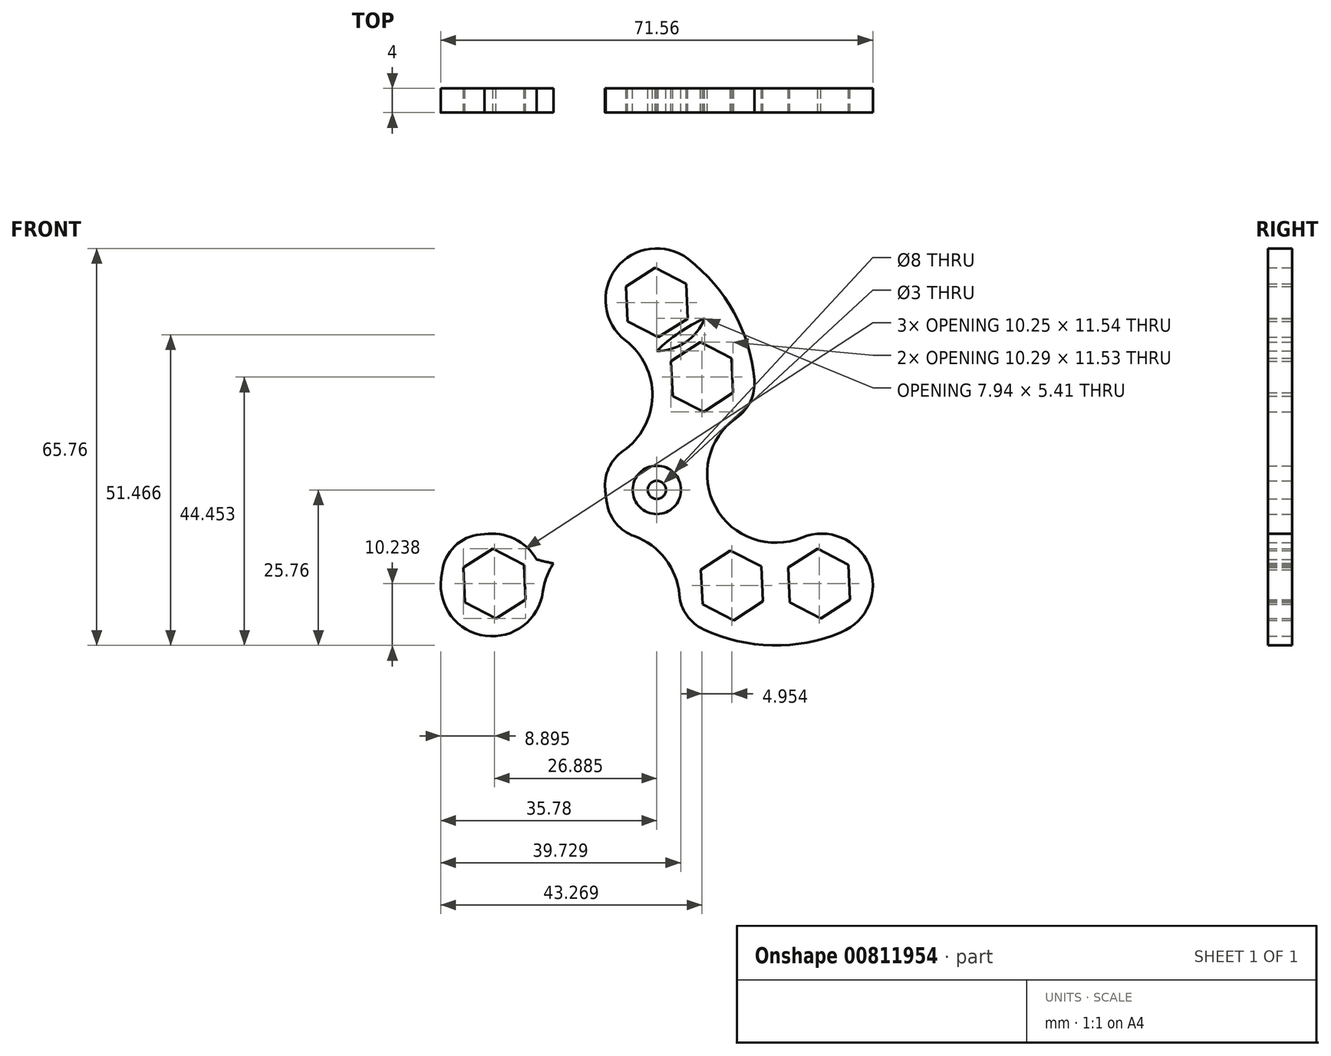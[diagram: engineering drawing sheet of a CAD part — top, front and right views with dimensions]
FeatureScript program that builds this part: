
annotation { "Feature Type Name" : "Feature", "Feature Type Description" : "" }
export const myFeature = defineFeature(function(context is Context, id is Id, definition is map)
    precondition{}
    {
        {
            var Q0;
            Q0=qCreatedBy(makeId("Front.planeOp"),FACE);
            var sketch = newSketch(context, id + "F0", { "sketchPlane" : qUnion([Q0])});
            skCircle(sketch, "E0", {"center": v(0, 0) * mm, "radius": 4 * mm});
            skCircle(sketch, "E1", {"center": v(0, 0) * mm, "radius": 1.5 * mm});
            skCircle(sketch, "E2", {"center": v(0, 0) * mm, "radius": 40 * mm, "construction": true});
            skCircle(sketch, "E3", {"center": v(0, 31.5) * mm, "radius": 8.5 * mm});
            skCircle(sketch, "E4", {"center": v(0, 0) * mm, "radius": 8.5 * mm});
            skCircle(sketch, "E5", {"center": v(-12.1, 15.75) * mm, "radius": 11.36 * mm});
            skCircle(sketch, "E6", {"center": v(-12.1, 15.75) * mm, "radius": 28.36 * mm});
            skCircle(sketch, "E7.1.0", {"center": v(-27.28, -15.75) * mm, "radius": 8.5 * mm});
            skCircle(sketch, "E7.2.0", {"center": v(27.28, -15.75) * mm, "radius": 8.5 * mm});
            skCircle(sketch, "E8.1.0", {"center": v(-7.59, -18.36) * mm, "radius": 11.36 * mm});
            skCircle(sketch, "E8.2.0", {"center": v(19.7, 2.6) * mm, "radius": 11.36 * mm});
            skCircle(sketch, "E9.1.0", {"center": v(-7.59, -18.36) * mm, "radius": 28.36 * mm});
            skCircle(sketch, "E9.2.0", {"center": v(19.7, 2.6) * mm, "radius": 28.36 * mm});
            skSolve(sketch);
        }
        {
            var Q0;
            Q0=makeQuery(id+"F0.imprint","IMPRINT",FACE,{"disambiguationData":[TD([[makeQuery(id+"F0.imprint","IMPRINT",EDGE,{"derivedFrom":sQuery(id+"F0.wireOp",EDGE,"E0")}),1.0]])]});
            extrude(context, id + "F1", {"entities" : qUnion([Q0]), "depth" : 4 * mm, "offsetDistance" : 25 * mm});
        }
        {
            var Q0;
            {var subQ0=sQuery(id+"F0.wireOp",EDGE,"E9.1.0");var subQ1=sQuery(id+"F0.wireOp",EDGE,"E4");var subQ2=makeQuery(id+"F0.imprint","INTERSECT",VERTEX,{"derivedFrom":[subQ1,subQ0]});Q0=makeQuery(id+"F0.imprint","IMPRINT",FACE,{"disambiguationData":[TD([[makeQuery(id+"F0.imprint","IMPRINT",EDGE,{"disambiguationData":[TD([[subQ2,1.0]])],"derivedFrom":subQ1}),-1.0]])]});}
            var Q1;
            {var subQ0=sQuery(id+"F0.wireOp",EDGE,"E9.1.0");var subQ1=sQuery(id+"F0.wireOp",EDGE,"E4");var subQ2=makeQuery(id+"F0.imprint","INTERSECT",VERTEX,{"derivedFrom":[subQ1,subQ0]});Q1=makeQuery(id+"F0.imprint","IMPRINT",FACE,{"disambiguationData":[TD([[makeQuery(id+"F0.imprint","IMPRINT",EDGE,{"disambiguationData":[TD([[subQ2,-1.0]])],"derivedFrom":subQ1}),-1.0]])]});}
            var Q2;
            {var subQ0=sQuery(id+"F0.wireOp",EDGE,"E5");var subQ1=sQuery(id+"F0.wireOp",EDGE,"E4");var subQ2=makeQuery(id+"F0.imprint","INTERSECT",VERTEX,{"derivedFrom":[subQ1,subQ0]});Q2=makeQuery(id+"F0.imprint","IMPRINT",FACE,{"disambiguationData":[TD([[makeQuery(id+"F0.imprint","IMPRINT",EDGE,{"disambiguationData":[TD([[subQ2,-1.0]])],"derivedFrom":subQ1}),-1.0]])]});}
            var Q3;
            {var subQ0=sQuery(id+"F0.wireOp",EDGE,"E9.2.0");var subQ1=sQuery(id+"F0.wireOp",EDGE,"E4");var subQ2=makeQuery(id+"F0.imprint","INTERSECT",VERTEX,{"derivedFrom":[subQ1,subQ0]});Q3=makeQuery(id+"F0.imprint","IMPRINT",FACE,{"disambiguationData":[TD([[makeQuery(id+"F0.imprint","IMPRINT",EDGE,{"disambiguationData":[TD([[subQ2,-1.0]])],"derivedFrom":subQ1}),-1.0]])]});}
            var Q4;
            {var subQ0=sQuery(id+"F0.wireOp",EDGE,"E8.1.0");var subQ1=sQuery(id+"F0.wireOp",EDGE,"E4");var subQ2=makeQuery(id+"F0.imprint","INTERSECT",VERTEX,{"derivedFrom":[subQ1,subQ0]});Q4=makeQuery(id+"F0.imprint","IMPRINT",FACE,{"disambiguationData":[TD([[makeQuery(id+"F0.imprint","IMPRINT",EDGE,{"disambiguationData":[TD([[subQ2,-1.0]])],"derivedFrom":subQ1}),-1.0]])]});}
            var Q5;
            {var subQ0=sQuery(id+"F0.wireOp",EDGE,"E8.2.0");var subQ1=sQuery(id+"F0.wireOp",EDGE,"E4");var subQ2=makeQuery(id+"F0.imprint","INTERSECT",VERTEX,{"derivedFrom":[subQ1,subQ0]});Q5=makeQuery(id+"F0.imprint","IMPRINT",FACE,{"disambiguationData":[TD([[makeQuery(id+"F0.imprint","IMPRINT",EDGE,{"disambiguationData":[TD([[subQ2,1.0]])],"derivedFrom":subQ1}),-1.0]])]});}
            var Q6;
            {var subQ6=sQuery(id+"F0.wireOp",EDGE,"E9.2.0");var subQ11=sQuery(id+"F0.wireOp",EDGE,"E3");var subQ12=makeQuery(id+"F0.imprint","INTERSECT",VERTEX,{"disambiguationData":[OD(0.0)],"derivedFrom":[subQ11,subQ6]});Q6=makeQuery(id+"F0.imprint","IMPRINT",FACE,{"disambiguationData":[TD([[makeQuery(id+"F0.imprint","IMPRINT",EDGE,{"disambiguationData":[TD([[subQ12,-1.0]])],"derivedFrom":subQ11}),-1.0]])]});}
            var Q7;
            {var subQ0=sQuery(id+"F0.wireOp",EDGE,"E9.2.0");var subQ1=sQuery(id+"F0.wireOp",EDGE,"E3");var subQ2=makeQuery(id+"F0.imprint","INTERSECT",VERTEX,{"disambiguationData":[OD(0.0)],"derivedFrom":[subQ1,subQ0]});Q7=makeQuery(id+"F0.imprint","IMPRINT",FACE,{"disambiguationData":[TD([[makeQuery(id+"F0.imprint","IMPRINT",EDGE,{"disambiguationData":[TD([[subQ2,-1.0]])],"derivedFrom":subQ1}),1.0]])]});}
            var Q8;
            {var subQ0=sQuery(id+"F0.wireOp",EDGE,"E3");var subQ1=makeQuery(id+"F0.imprint","INTERSECT",VERTEX,{"derivedFrom":[subQ0,sQuery(id+"F0.wireOp",EDGE,"E6")]});Q8=makeQuery(id+"F0.imprint","IMPRINT",FACE,{"disambiguationData":[TD([[makeQuery(id+"F0.imprint","IMPRINT",EDGE,{"disambiguationData":[TD([[subQ1,-1.0]])],"derivedFrom":subQ0}),1.0]])]});}
            var Q9;
            {var subQ0=sQuery(id+"F0.wireOp",EDGE,"E6");var subQ1=sQuery(id+"F0.wireOp",EDGE,"E3");var subQ2=makeQuery(id+"F0.imprint","INTERSECT",VERTEX,{"derivedFrom":[subQ1,subQ0]});Q9=makeQuery(id+"F0.imprint","IMPRINT",FACE,{"disambiguationData":[TD([[makeQuery(id+"F0.imprint","IMPRINT",EDGE,{"disambiguationData":[TD([[subQ2,1.0]])],"derivedFrom":subQ1}),-1.0]])]});}
            var Q10;
            {var subQ0=sQuery(id+"F0.wireOp",EDGE,"E5");var subQ1=sQuery(id+"F0.wireOp",EDGE,"E3");var subQ2=makeQuery(id+"F0.imprint","INTERSECT",VERTEX,{"derivedFrom":[subQ1,subQ0]});Q10=makeQuery(id+"F0.imprint","IMPRINT",FACE,{"disambiguationData":[TD([[makeQuery(id+"F0.imprint","IMPRINT",EDGE,{"disambiguationData":[TD([[subQ2,-1.0]])],"derivedFrom":subQ1}),-1.0]])]});}
            var Q11;
            {var subQ0=sQuery(id+"F0.wireOp",EDGE,"E7.2.0");var subQ1=makeQuery(id+"F0.imprint","INTERSECT",VERTEX,{"derivedFrom":[subQ0,sQuery(id+"F0.wireOp",EDGE,"E9.2.0")]});Q11=makeQuery(id+"F0.imprint","IMPRINT",FACE,{"disambiguationData":[TD([[makeQuery(id+"F0.imprint","IMPRINT",EDGE,{"disambiguationData":[TD([[subQ1,-1.0]])],"derivedFrom":subQ0}),1.0]])]});}
            var Q12;
            {var subQ0=sQuery(id+"F0.wireOp",EDGE,"E9.1.0");var subQ1=sQuery(id+"F0.wireOp",EDGE,"E7.2.0");var subQ2=makeQuery(id+"F0.imprint","INTERSECT",VERTEX,{"disambiguationData":[OD(0.0)],"derivedFrom":[subQ1,subQ0]});Q12=makeQuery(id+"F0.imprint","IMPRINT",FACE,{"disambiguationData":[TD([[makeQuery(id+"F0.imprint","IMPRINT",EDGE,{"disambiguationData":[TD([[subQ2,-1.0]])],"derivedFrom":subQ1}),1.0]])]});}
            var Q13;
            {var subQ0=sQuery(id+"F0.wireOp",EDGE,"E8.2.0");var subQ1=sQuery(id+"F0.wireOp",EDGE,"E7.2.0");var subQ2=makeQuery(id+"F0.imprint","INTERSECT",VERTEX,{"derivedFrom":[subQ1,subQ0]});Q13=makeQuery(id+"F0.imprint","IMPRINT",FACE,{"disambiguationData":[TD([[makeQuery(id+"F0.imprint","IMPRINT",EDGE,{"disambiguationData":[TD([[subQ2,-1.0]])],"derivedFrom":subQ1}),-1.0]])]});}
            var Q14;
            {var subQ4=sQuery(id+"F0.wireOp",EDGE,"E6");var subQ5=makeQuery(id+"F0.imprint","INTERSECT",VERTEX,{"derivedFrom":[sQuery(id+"F0.wireOp",EDGE,"E4"),subQ4]});Q14=makeQuery(id+"F0.imprint","IMPRINT",FACE,{"disambiguationData":[TD([[makeQuery(id+"F0.imprint","IMPRINT",EDGE,{"disambiguationData":[TD([[subQ5,1.0]])],"derivedFrom":subQ4}),-1.0]])]});}
            var Q15;
            {var subQ0=sQuery(id+"F0.wireOp",EDGE,"E9.2.0");var subQ1=sQuery(id+"F0.wireOp",EDGE,"E7.2.0");var subQ2=makeQuery(id+"F0.imprint","INTERSECT",VERTEX,{"derivedFrom":[subQ1,subQ0]});Q15=makeQuery(id+"F0.imprint","IMPRINT",FACE,{"disambiguationData":[TD([[makeQuery(id+"F0.imprint","IMPRINT",EDGE,{"disambiguationData":[TD([[subQ2,1.0]])],"derivedFrom":subQ1}),-1.0]])]});}
            var Q16;
            {var subQ0=sQuery(id+"F0.wireOp",EDGE,"E7.1.0");var subQ1=sQuery(id+"F0.wireOp",EDGE,"E6");var subQ2=makeQuery(id+"F0.imprint","INTERSECT",VERTEX,{"disambiguationData":[OD(0.0)],"derivedFrom":[subQ1,subQ0]});Q16=makeQuery(id+"F0.imprint","IMPRINT",FACE,{"disambiguationData":[TD([[makeQuery(id+"F0.imprint","IMPRINT",EDGE,{"disambiguationData":[TD([[subQ2,-1.0]])],"derivedFrom":subQ1}),-1.0]])]});}
            var Q17;
            {var subQ0=sQuery(id+"F0.wireOp",EDGE,"E9.1.0");var subQ1=sQuery(id+"F0.wireOp",EDGE,"E6");var subQ2=makeQuery(id+"F0.imprint","INTERSECT",VERTEX,{"disambiguationData":[OD(0.0)],"derivedFrom":[subQ1,subQ0]});Q17=makeQuery(id+"F0.imprint","IMPRINT",FACE,{"disambiguationData":[TD([[makeQuery(id+"F0.imprint","IMPRINT",EDGE,{"disambiguationData":[TD([[subQ2,-1.0]])],"derivedFrom":subQ1}),-1.0]])]});}
            var Q18;
            {var subQ8=sQuery(id+"F0.wireOp",EDGE,"E9.1.0");var subQ10=sQuery(id+"F0.wireOp",EDGE,"E5");var subQ11=makeQuery(id+"F0.imprint","INTERSECT",VERTEX,{"disambiguationData":[OD(0.0)],"derivedFrom":[subQ10,subQ8]});Q18=makeQuery(id+"F0.imprint","IMPRINT",FACE,{"disambiguationData":[TD([[makeQuery(id+"F0.imprint","IMPRINT",EDGE,{"disambiguationData":[TD([[subQ11,-1.0]])],"derivedFrom":subQ10}),-1.0]])]});}
            var Q19;
            {var subQ0=sQuery(id+"F0.wireOp",EDGE,"E7.1.0");var subQ1=sQuery(id+"F0.wireOp",EDGE,"E6");var subQ2=makeQuery(id+"F0.imprint","INTERSECT",VERTEX,{"disambiguationData":[OD(0.0)],"derivedFrom":[subQ1,subQ0]});Q19=makeQuery(id+"F0.imprint","IMPRINT",FACE,{"disambiguationData":[TD([[makeQuery(id+"F0.imprint","IMPRINT",EDGE,{"disambiguationData":[TD([[subQ2,-1.0]])],"derivedFrom":subQ1}),1.0]])]});}
            var Q20;
            {var subQ0=sQuery(id+"F0.wireOp",EDGE,"E7.1.0");var subQ1=sQuery(id+"F0.wireOp",EDGE,"E6");var subQ2=makeQuery(id+"F0.imprint","INTERSECT",VERTEX,{"disambiguationData":[OD(1.0)],"derivedFrom":[subQ1,subQ0]});Q20=makeQuery(id+"F0.imprint","IMPRINT",FACE,{"disambiguationData":[TD([[makeQuery(id+"F0.imprint","IMPRINT",EDGE,{"disambiguationData":[TD([[subQ2,-1.0]])],"derivedFrom":subQ1}),-1.0]])]});}
            var Q21;
            Q21=makeQuery(id+"F0.imprint","IMPRINT",FACE,{"disambiguationData":[TD([[makeQuery(id+"F0.imprint","IMPRINT",EDGE,{"derivedFrom":sQuery(id+"F0.wireOp",EDGE,"E0")}),-1.0]])]});
            extrude(context, id + "F2", {"entities" : qUnion([Q0, Q1, Q2, Q3, Q4, Q5, Q6, Q7, Q8, Q9, Q10, Q11, Q12, Q13, Q14, Q15, Q16, Q17, Q18, Q19, Q20, Q21]), "depth" : 4 * mm, "offsetDistance" : 25 * mm});
        }
        {
            var Q0;
            Q0=makeQuery(id+"F2.opExtrude","SWEPT_EDGE",EDGE,{"disambiguationData":[OSD([sQuery(id+"F0.wireOp",EDGE,"E6"),sQuery(id+"F0.wireOp",EDGE,"E8.2.0")])]});
            var Q1;
            Q1=makeQuery(id+"F2.opExtrude","SWEPT_EDGE",EDGE,{"disambiguationData":[OSD([sQuery(id+"F0.wireOp",EDGE,"E5"),sQuery(id+"F0.wireOp",EDGE,"E9.1.0")])]});
            var Q2;
            Q2=makeQuery(id+"F2.opExtrude","SWEPT_EDGE",EDGE,{"disambiguationData":[OSD([sQuery(id+"F0.wireOp",EDGE,"E8.1.0"),sQuery(id+"F0.wireOp",EDGE,"E9.2.0")])]});
            fillet(context, id + "F3", {"entities" : qUnion([Q0, Q1, Q2]), "radius" : 7 * mm, "tangentPropagation" : true, "allowEdgeOverflow" : false});
        }
        {
            var Q0;
            Q0=qCreatedBy(makeId("Front.planeOp"),FACE);
            var sketch = newSketch(context, id + "F4", { "sketchPlane" : qUnion([Q0])});
            skCircle(sketch, "E10.cCircle", {"center": v(-19.93, -2.86) * mm, "radius": 5 * mm, "construction": true});
            skLineSegment(sketch, "E10.0", {"start": v(-20.24, 2.9) * mm, "end": v(-15.1, 0.29) * mm});
            skLineSegment(sketch, "E10.1", {"start": v(-15.1, 0.29) * mm, "end": v(-14.79, -5.48) * mm});
            skLineSegment(sketch, "E10.2", {"start": v(-14.79, -5.48) * mm, "end": v(-19.63, -8.63) * mm});
            skLineSegment(sketch, "E10.3", {"start": v(-19.63, -8.63) * mm, "end": v(-24.77, -6) * mm});
            skLineSegment(sketch, "E10.4", {"start": v(-24.77, -6) * mm, "end": v(-25.08, -0.24) * mm});
            skLineSegment(sketch, "E10.5", {"start": v(-25.08, -0.24) * mm, "end": v(-20.24, 2.9) * mm});
            skPoint(sketch, "E10.0.midPoint", {"position": v(-17.67, 1.6) * mm});
            skCircle(sketch, "E11.cCircle", {"center": v(0, 31.04) * mm, "radius": 5 * mm, "construction": true});
            skLineSegment(sketch, "E11.0", {"start": v(5.12, 28.38) * mm, "end": v(0.26, 25.28) * mm});
            skLineSegment(sketch, "E11.1", {"start": v(0.26, 25.28) * mm, "end": v(-4.87, 27.94) * mm});
            skLineSegment(sketch, "E11.2", {"start": v(-4.87, 27.94) * mm, "end": v(-5.12, 33.7) * mm});
            skLineSegment(sketch, "E11.3", {"start": v(-5.12, 33.7) * mm, "end": v(-0.26, 36.81) * mm});
            skLineSegment(sketch, "E11.4", {"start": v(-0.26, 36.81) * mm, "end": v(4.87, 34.15) * mm});
            skLineSegment(sketch, "E11.5", {"start": v(4.87, 34.15) * mm, "end": v(5.12, 28.38) * mm});
            skPoint(sketch, "E11.0.midPoint", {"position": v(2.7, 26.83) * mm});
            skPoint(sketch, "E12.1.0", {"position": v(-24.58, -11.08) * mm});
            skCircle(sketch, "E12.1.1", {"center": v(-26.88, -15.52) * mm, "radius": 5 * mm, "construction": true});
            skLineSegment(sketch, "E12.1.2", {"start": v(-31.75, -18.63) * mm, "end": v(-32, -12.86) * mm});
            skLineSegment(sketch, "E12.1.3", {"start": v(-21.76, -18.18) * mm, "end": v(-26.63, -21.29) * mm});
            skLineSegment(sketch, "E12.1.4", {"start": v(-22.02, -12.41) * mm, "end": v(-21.76, -18.18) * mm});
            skLineSegment(sketch, "E12.1.5", {"start": v(-27.14, -9.75) * mm, "end": v(-22.02, -12.41) * mm});
            skLineSegment(sketch, "E12.1.6", {"start": v(-26.63, -21.29) * mm, "end": v(-31.75, -18.63) * mm});
            skLineSegment(sketch, "E12.1.7", {"start": v(-32, -12.86) * mm, "end": v(-27.14, -9.75) * mm});
            skLineSegment(sketch, "E12.1.8", {"start": v(17.28, -12.69) * mm, "end": v(17.59, -18.45) * mm});
            skCircle(sketch, "E12.1.9", {"center": v(12.44, -15.83) * mm, "radius": 5 * mm, "construction": true});
            skPoint(sketch, "E12.1.10", {"position": v(7.45, -16.1) * mm});
            skLineSegment(sketch, "E12.1.11", {"start": v(12.75, -21.6) * mm, "end": v(7.6, -18.98) * mm});
            skLineSegment(sketch, "E12.1.12", {"start": v(17.59, -18.45) * mm, "end": v(12.75, -21.6) * mm});
            skLineSegment(sketch, "E12.1.13", {"start": v(12.14, -10.07) * mm, "end": v(17.28, -12.69) * mm});
            skLineSegment(sketch, "E12.1.14", {"start": v(7.3, -13.21) * mm, "end": v(12.14, -10.07) * mm});
            skLineSegment(sketch, "E12.1.15", {"start": v(7.6, -18.98) * mm, "end": v(7.3, -13.21) * mm});
            skPoint(sketch, "E12.2.0", {"position": v(21.89, -15.75) * mm});
            skCircle(sketch, "E12.2.1", {"center": v(26.88, -15.52) * mm, "radius": 5 * mm, "construction": true});
            skLineSegment(sketch, "E12.2.2", {"start": v(32, -18.18) * mm, "end": v(27.14, -21.29) * mm});
            skLineSegment(sketch, "E12.2.3", {"start": v(26.63, -9.75) * mm, "end": v(31.75, -12.41) * mm});
            skLineSegment(sketch, "E12.2.4", {"start": v(21.76, -12.86) * mm, "end": v(26.63, -9.75) * mm});
            skLineSegment(sketch, "E12.2.5", {"start": v(22.02, -18.63) * mm, "end": v(21.76, -12.86) * mm});
            skLineSegment(sketch, "E12.2.6", {"start": v(31.75, -12.41) * mm, "end": v(32, -18.18) * mm});
            skLineSegment(sketch, "E12.2.7", {"start": v(27.14, -21.29) * mm, "end": v(22.02, -18.63) * mm});
            skLineSegment(sketch, "E12.2.8", {"start": v(2.34, 21.31) * mm, "end": v(7.18, 24.46) * mm});
            skCircle(sketch, "E12.2.9", {"center": v(7.49, 18.7) * mm, "radius": 5 * mm, "construction": true});
            skPoint(sketch, "E12.2.10", {"position": v(10.21, 14.5) * mm});
            skLineSegment(sketch, "E12.2.11", {"start": v(12.33, 21.84) * mm, "end": v(12.64, 16.07) * mm});
            skLineSegment(sketch, "E12.2.12", {"start": v(7.18, 24.46) * mm, "end": v(12.33, 21.84) * mm});
            skLineSegment(sketch, "E12.2.13", {"start": v(2.65, 15.55) * mm, "end": v(2.34, 21.31) * mm});
            skLineSegment(sketch, "E12.2.14", {"start": v(7.8, 12.93) * mm, "end": v(2.65, 15.55) * mm});
            skLineSegment(sketch, "E12.2.15", {"start": v(12.64, 16.07) * mm, "end": v(7.8, 12.93) * mm});
            skPoint(sketch, "E12.center", {"position": v(0, 0) * mm});
            skSolve(sketch);
        }
        {
            var Q0;
            Q0=makeQuery(id+"F4.imprint","IMPRINT",FACE,{"disambiguationData":[TD([[makeQuery(id+"F4.imprint","IMPRINT",EDGE,{"derivedFrom":sQuery(id+"F4.wireOp",EDGE,"E11.0")}),-1.0]])]});
            var Q1;
            Q1=makeQuery(id+"F4.imprint","IMPRINT",FACE,{"disambiguationData":[TD([[makeQuery(id+"F4.imprint","IMPRINT",EDGE,{"derivedFrom":sQuery(id+"F4.wireOp",EDGE,"E12.2.8")}),-1.0]])]});
            var Q2;
            Q2=makeQuery(id+"F4.imprint","IMPRINT",FACE,{"disambiguationData":[TD([[makeQuery(id+"F4.imprint","IMPRINT",EDGE,{"derivedFrom":sQuery(id+"F4.wireOp",EDGE,"E12.2.2")}),-1.0]])]});
            var Q3;
            Q3=makeQuery(id+"F4.imprint","IMPRINT",FACE,{"disambiguationData":[TD([[makeQuery(id+"F4.imprint","IMPRINT",EDGE,{"derivedFrom":sQuery(id+"F4.wireOp",EDGE,"E12.1.8")}),-1.0]])]});
            var Q4;
            Q4=makeQuery(id+"F4.imprint","IMPRINT",FACE,{"disambiguationData":[TD([[makeQuery(id+"F4.imprint","IMPRINT",EDGE,{"derivedFrom":sQuery(id+"F4.wireOp",EDGE,"E10.0")}),-1.0]])]});
            var Q5;
            Q5=makeQuery(id+"F4.imprint","IMPRINT",FACE,{"disambiguationData":[TD([[makeQuery(id+"F4.imprint","IMPRINT",EDGE,{"derivedFrom":sQuery(id+"F4.wireOp",EDGE,"E12.1.2")}),-1.0]])]});
            extrude(context, id + "F5", {"entities" : qUnion([Q0, Q1, Q2, Q3, Q4, Q5]), "operationType" : NewBodyOperationType.REMOVE, "depth" : 5 * mm, "offsetDistance" : 25 * mm});
        }
    });
